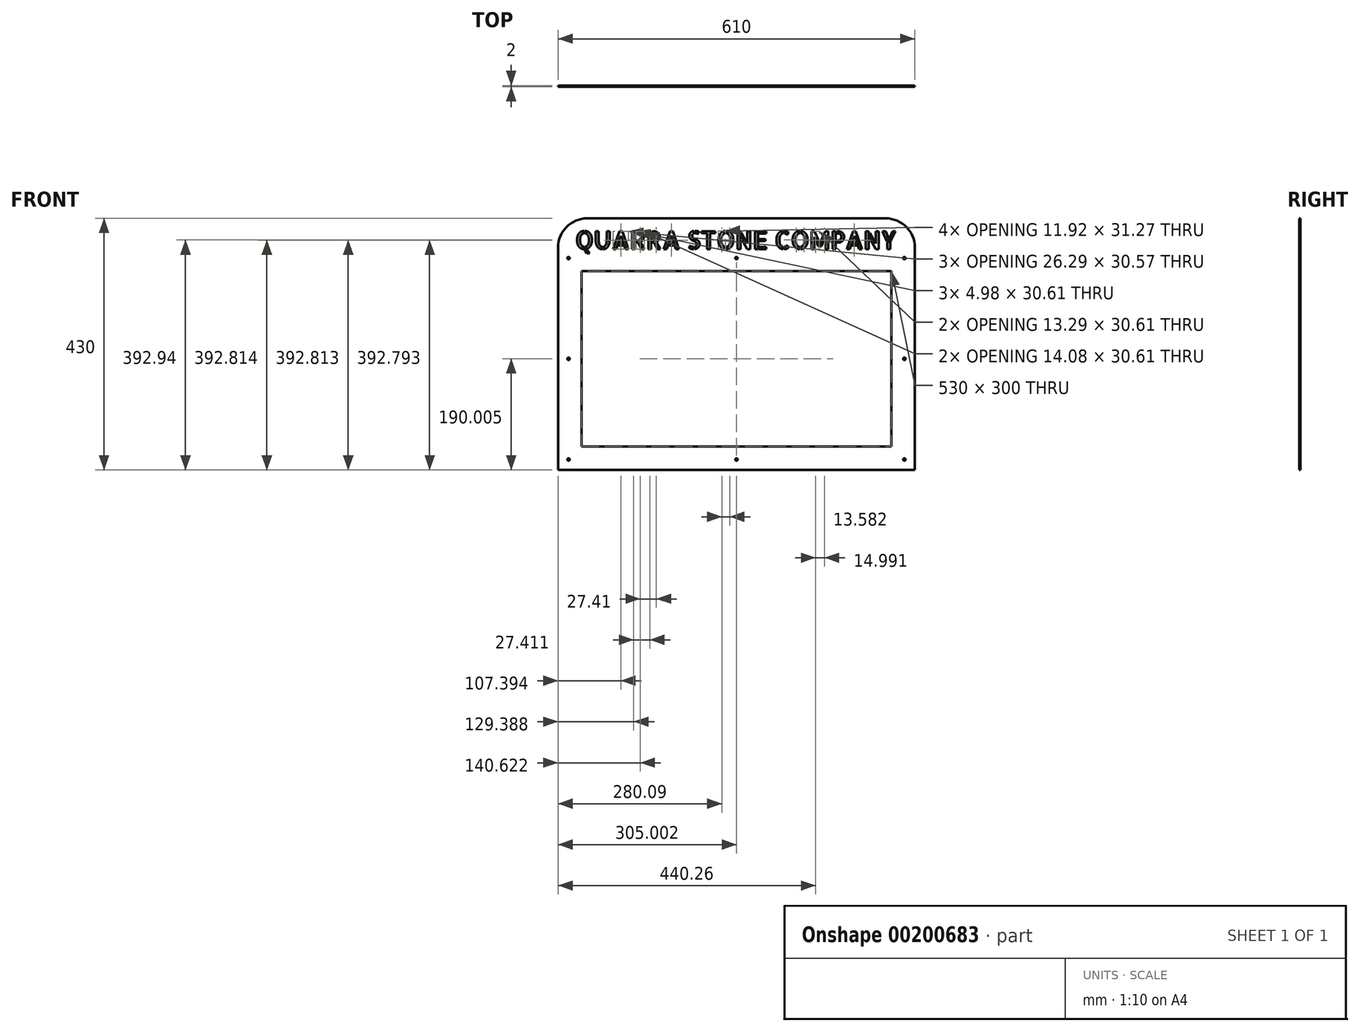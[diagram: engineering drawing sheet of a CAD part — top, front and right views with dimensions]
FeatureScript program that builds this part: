
annotation { "Feature Type Name" : "Feature", "Feature Type Description" : "" }
export const myFeature = defineFeature(function(context is Context, id is Id, definition is map)
    precondition{}
    {
        {
            var Q0;
            Q0=qCreatedBy(makeId("Front.planeOp"),FACE);
            var sketch = newSketch(context, id + "F0", { "sketchPlane" : qUnion([Q0])});
            skLineSegment(sketch, "E0.bottom", {"start": v(-411.5, 274.1) * mm, "end": v(118.5, 274.1) * mm});
            skLineSegment(sketch, "E0.top", {"start": v(-411.5, -25.9) * mm, "end": v(118.5, -25.9) * mm});
            skLineSegment(sketch, "E0.left", {"start": v(-411.5, 274.1) * mm, "end": v(-411.5, -25.9) * mm});
            skLineSegment(sketch, "E0.right", {"start": v(118.5, 274.1) * mm, "end": v(118.5, -25.9) * mm});
            skLineSegment(sketch, "E1", {"start": v(158.5, 314.1) * mm, "end": v(158.5, -65.9) * mm});
            skLineSegment(sketch, "E2", {"start": v(158.5, -65.9) * mm, "end": v(-451.5, -65.9) * mm});
            skLineSegment(sketch, "E3", {"start": v(-451.5, 314.1) * mm, "end": v(-451.5, -65.9) * mm});
            skPoint(sketch, "E4", {"position": v(-433.5, 296.1) * mm});
            skPoint(sketch, "E5", {"position": v(140.5, 296.1) * mm});
            skPoint(sketch, "E6", {"position": v(-433.5, -47.9) * mm});
            skPoint(sketch, "E7", {"position": v(140.5, -47.9) * mm});
            skCircle(sketch, "E8", {"center": v(-433.5, 296.1) * mm, "radius": 2 * mm});
            skCircle(sketch, "E9", {"center": v(-433.5, -47.9) * mm, "radius": 2 * mm});
            skCircle(sketch, "E10", {"center": v(140.5, -47.9) * mm, "radius": 2 * mm});
            skCircle(sketch, "E11", {"center": v(140.5, 296.1) * mm, "radius": 2 * mm});
            skPoint(sketch, "E12", {"position": v(-146.5, 296.1) * mm});
            skPoint(sketch, "E13", {"position": v(-146.5, -47.9) * mm});
            skPoint(sketch, "E13.positionSnap0", {"position": v(-146.5, -65.9) * mm});
            skPoint(sketch, "E14", {"position": v(-433.5, 124.1) * mm});
            skPoint(sketch, "E14.positionSnap0", {"position": v(-451.5, 124.1) * mm});
            skPoint(sketch, "E15", {"position": v(140.5, 124.1) * mm});
            skPoint(sketch, "E15.positionSnap0", {"position": v(-411.5, 124.1) * mm});
            skCircle(sketch, "E16", {"center": v(-433.5, 124.1) * mm, "radius": 2 * mm});
            skCircle(sketch, "E17", {"center": v(-146.5, 296.1) * mm, "radius": 2 * mm});
            skCircle(sketch, "E18", {"center": v(140.5, 124.1) * mm, "radius": 2 * mm});
            skCircle(sketch, "E19", {"center": v(-146.5, -47.9) * mm, "radius": 2 * mm});
            skLineSegment(sketch, "E20.top", {"start": v(-401.5, 364.1) * mm, "end": v(108.5, 364.1) * mm});
            skLineSegment(sketch, "E20.left", {"start": v(-451.5, 314.1) * mm, "end": v(-451.5, 314.1) * mm});
            skLineSegment(sketch, "E20.right", {"start": v(158.5, 314.1) * mm, "end": v(158.5, 314.1) * mm});
            skText(sketch, "E21", { "text": "QUARRA STONE COMPANY", "fontName": "AllertaStencil-Regular.ttf"});
            skPoint(sketch, "E22.visualSharp", {"position": v(-451.5, 364.1) * mm});
            skArc(sketch, "E22.filletArc", {"start": v(-401.5, 364.1) * mm, "mid": v(-436.86, 349.45) * mm, "end": v(-451.5, 314.1) * mm});
            skPoint(sketch, "E23.visualSharp", {"position": v(158.5, 364.1) * mm});
            skArc(sketch, "E23.filletArc", {"start": v(158.5, 314.1) * mm, "mid": v(143.85, 349.45) * mm, "end": v(108.5, 364.1) * mm});
            const initialGuessF0  = {"E21": [-0.42159, 0.3116, 1, 0, 0.03062]};
            skSetInitialGuess(sketch, initialGuessF0);
            skSolve(sketch);
        }
        {
            var Q0;
            Q0 = qSketchRegion(id + "F0", true);
            extrude(context, id + "F1", {"entities" : qUnion([Q0]), "depth" : 2 * mm});
        }
    });
